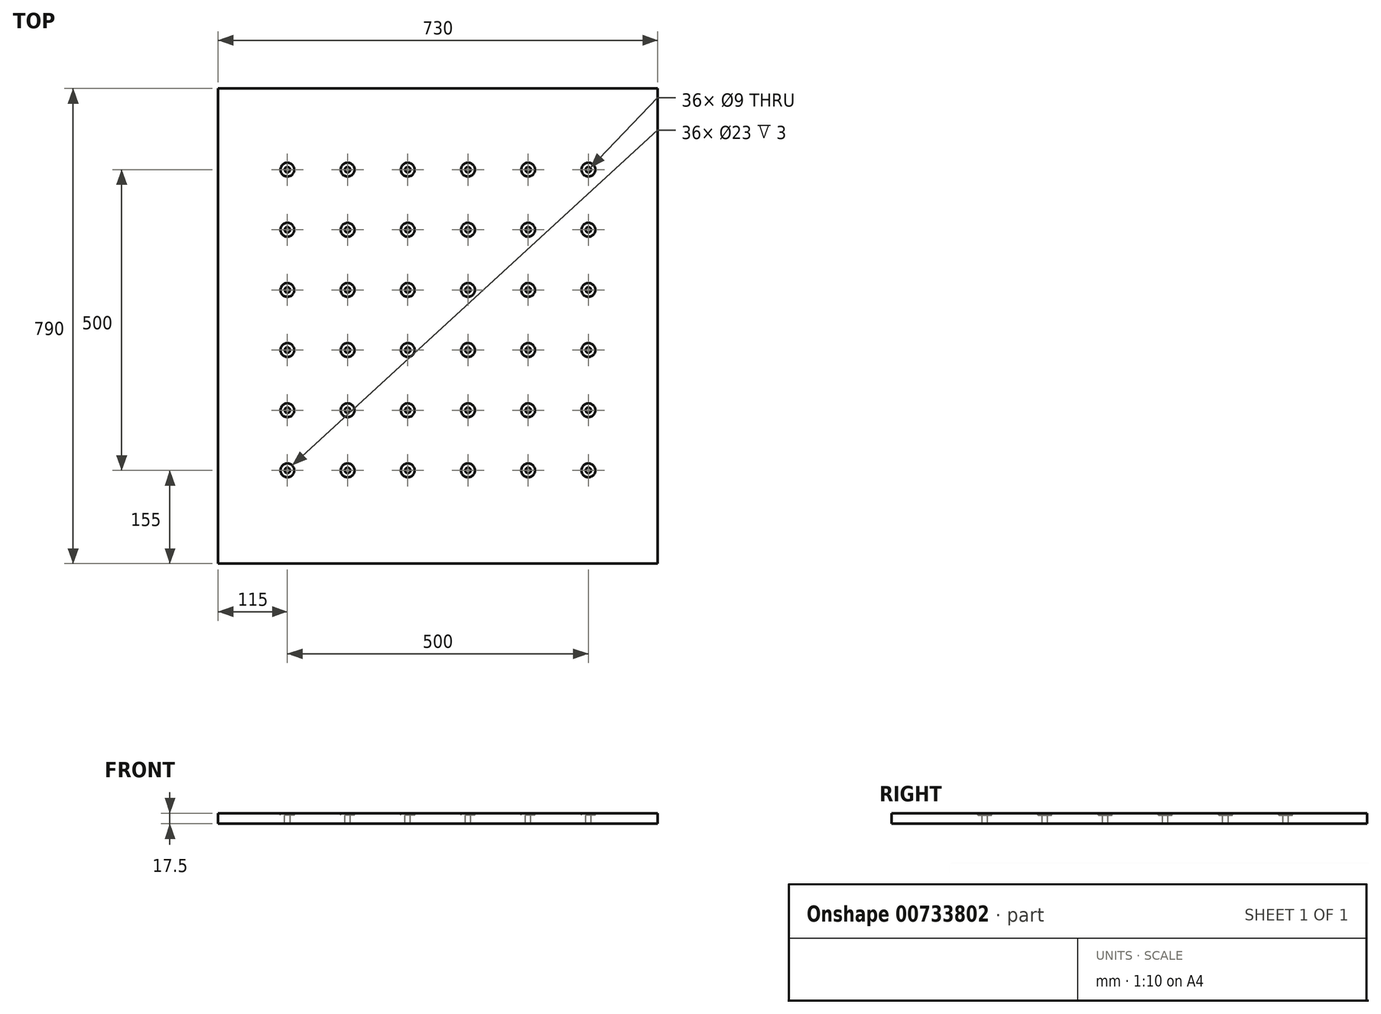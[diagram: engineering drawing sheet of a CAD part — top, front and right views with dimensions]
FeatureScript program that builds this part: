
annotation { "Feature Type Name" : "Feature", "Feature Type Description" : "" }
export const myFeature = defineFeature(function(context is Context, id is Id, definition is map)
    precondition{}
    {
        {
            var Q0;
            Q0=qCreatedBy(makeId("Top.planeOp"),FACE);
            var sketch = newSketch(context, id + "F0", { "sketchPlane" : qUnion([Q0])});
            skLineSegment(sketch, "E0.bottom", {"start": v(365, -395) * mm, "end": v(-365, -395) * mm});
            skLineSegment(sketch, "E0.top", {"start": v(365, 395) * mm, "end": v(-365, 395) * mm});
            skLineSegment(sketch, "E0.left", {"start": v(365, -395) * mm, "end": v(365, 395) * mm});
            skLineSegment(sketch, "E0.right", {"start": v(-365, -395) * mm, "end": v(-365, 395) * mm});
            skPoint(sketch, "E0.middle", {"position": v(0, 0) * mm});
            skSolve(sketch);
        }
        {
            var Q0;
            Q0 = qSketchRegion(id + "F0", true);
            extrude(context, id + "F1", {"entities" : qUnion([Q0]), "depth" : 17.5 * mm, "offsetDistance" : 25 * mm});
        }
        {
            var Q0;
            Q0=makeQuery(id+"F1.opExtrude","CAP_FACE",FACE,{"disambiguationData":[OSD([sQuery(id+"F0.wireOp",EDGE,"E0.bottom"),sQuery(id+"F0.wireOp",EDGE,"E0.top"),sQuery(id+"F0.wireOp",EDGE,"E0.left"),sQuery(id+"F0.wireOp",EDGE,"E0.right")])],"isStart":false});
            var sketch = newSketch(context, id + "F2", { "sketchPlane" : qUnion([Q0])});
            skPoint(sketch, "E1", {"position": v(-250, 260) * mm});
            skPoint(sketch, "E2.0.1.0", {"position": v(-250, 160) * mm});
            skPoint(sketch, "E2.0.2.0", {"position": v(-250, 60) * mm});
            skPoint(sketch, "E2.0.3.0", {"position": v(-250, -40) * mm});
            skPoint(sketch, "E2.0.4.0", {"position": v(-250, -140) * mm});
            skPoint(sketch, "E2.1.0.0", {"position": v(-150, 260) * mm});
            skPoint(sketch, "E2.1.1.0", {"position": v(-150, 160) * mm});
            skPoint(sketch, "E2.1.2.0", {"position": v(-150, 60) * mm});
            skPoint(sketch, "E2.1.3.0", {"position": v(-150, -40) * mm});
            skPoint(sketch, "E2.1.4.0", {"position": v(-150, -140) * mm});
            skPoint(sketch, "E2.2.0.0", {"position": v(-50, 260) * mm});
            skPoint(sketch, "E2.2.1.0", {"position": v(-50, 160) * mm});
            skPoint(sketch, "E2.2.2.0", {"position": v(-50, 60) * mm});
            skPoint(sketch, "E2.2.3.0", {"position": v(-50, -40) * mm});
            skPoint(sketch, "E2.2.4.0", {"position": v(-50, -140) * mm});
            skPoint(sketch, "E2.3.0.0", {"position": v(50, 260) * mm});
            skPoint(sketch, "E2.3.1.0", {"position": v(50, 160) * mm});
            skPoint(sketch, "E2.3.2.0", {"position": v(50, 60) * mm});
            skPoint(sketch, "E2.3.3.0", {"position": v(50, -40) * mm});
            skPoint(sketch, "E2.3.4.0", {"position": v(50, -140) * mm});
            skPoint(sketch, "E2.4.0.0", {"position": v(150, 260) * mm});
            skPoint(sketch, "E2.4.1.0", {"position": v(150, 160) * mm});
            skPoint(sketch, "E2.4.2.0", {"position": v(150, 60) * mm});
            skPoint(sketch, "E2.4.3.0", {"position": v(150, -40) * mm});
            skPoint(sketch, "E2.4.4.0", {"position": v(150, -140) * mm});
            skLineSegment(sketch, "E2.direction1", {"start": v(-250, 260) * mm, "end": v(-150, 260) * mm, "construction": true});
            skLineSegment(sketch, "E2.direction2", {"start": v(-250, 260) * mm, "end": v(-250, 160) * mm, "construction": true});
            skPoint(sketch, "E3.0.5.0", {"position": v(250, 260) * mm});
            skPoint(sketch, "E3.0.5.1", {"position": v(250, 160) * mm});
            skPoint(sketch, "E3.0.5.2", {"position": v(250, 60) * mm});
            skPoint(sketch, "E3.0.5.3", {"position": v(250, -40) * mm});
            skPoint(sketch, "E3.0.5.4", {"position": v(250, -140) * mm});
            skPoint(sketch, "E4.0.0.5", {"position": v(-250, -240) * mm});
            skPoint(sketch, "E4.0.1.5", {"position": v(-150, -240) * mm});
            skPoint(sketch, "E4.0.2.5", {"position": v(-50, -240) * mm});
            skPoint(sketch, "E4.0.3.5", {"position": v(50, -240) * mm});
            skPoint(sketch, "E4.0.4.5", {"position": v(150, -240) * mm});
            skPoint(sketch, "E4.0.5.5", {"position": v(250, -240) * mm});
            skSolve(sketch);
        }
        {
            var Q0;
            Q0=sQuery(id+"F2.wireOp",VERTEX,"E1");
            var Q1;
            Q1=sQuery(id+"F2.wireOp",VERTEX,"E2.1.0.0");
            var Q2;
            Q2=sQuery(id+"F2.wireOp",VERTEX,"E2.2.0.0");
            var Q3;
            Q3=sQuery(id+"F2.wireOp",VERTEX,"E2.3.0.0");
            var Q4;
            Q4=sQuery(id+"F2.wireOp",VERTEX,"E2.4.0.0");
            var Q5;
            Q5=sQuery(id+"F2.wireOp",VERTEX,"E2.5.0.0");
            var Q6;
            Q6=sQuery(id+"F2.wireOp",VERTEX,"E2.1.1.0");
            var Q7;
            Q7=sQuery(id+"F2.wireOp",VERTEX,"E2.0.2.0");
            var Q8;
            Q8=sQuery(id+"F2.wireOp",VERTEX,"E2.0.1.0");
            var Q9;
            Q9=sQuery(id+"F2.wireOp",VERTEX,"E2.1.5.0");
            var Q10;
            Q10=sQuery(id+"F2.wireOp",VERTEX,"E2.4.2.0");
            var Q11;
            Q11=sQuery(id+"F2.wireOp",VERTEX,"E2.1.4.0");
            var Q12;
            Q12=sQuery(id+"F2.wireOp",VERTEX,"E2.0.6.0");
            var Q13;
            Q13=sQuery(id+"F2.wireOp",VERTEX,"E2.1.3.0");
            var Q14;
            Q14=sQuery(id+"F2.wireOp",VERTEX,"E2.4.4.0");
            var Q15;
            Q15=sQuery(id+"F2.wireOp",VERTEX,"E2.0.5.0");
            var Q16;
            Q16=sQuery(id+"F2.wireOp",VERTEX,"E2.3.4.0");
            var Q17;
            Q17=sQuery(id+"F2.wireOp",VERTEX,"E2.1.2.0");
            var Q18;
            Q18=sQuery(id+"F2.wireOp",VERTEX,"E2.5.6.0");
            var Q19;
            Q19=sQuery(id+"F2.wireOp",VERTEX,"E2.2.2.0");
            var Q20;
            Q20=sQuery(id+"F2.wireOp",VERTEX,"E2.3.6.0");
            var Q21;
            Q21=sQuery(id+"F2.wireOp",VERTEX,"E2.4.6.0");
            var Q22;
            Q22=sQuery(id+"F2.wireOp",VERTEX,"E2.2.4.0");
            var Q23;
            Q23=sQuery(id+"F2.wireOp",VERTEX,"E2.2.6.0");
            var Q24;
            Q24=sQuery(id+"F2.wireOp",VERTEX,"E2.0.4.0");
            var Q25;
            Q25=sQuery(id+"F2.wireOp",VERTEX,"E2.5.1.0");
            var Q26;
            Q26=sQuery(id+"F2.wireOp",VERTEX,"E2.3.1.0");
            var Q27;
            Q27=sQuery(id+"F2.wireOp",VERTEX,"E2.5.3.0");
            var Q28;
            Q28=sQuery(id+"F2.wireOp",VERTEX,"E2.3.3.0");
            var Q29;
            Q29=sQuery(id+"F2.wireOp",VERTEX,"E2.5.5.0");
            var Q30;
            Q30=sQuery(id+"F2.wireOp",VERTEX,"E2.0.3.0");
            var Q31;
            Q31=sQuery(id+"F2.wireOp",VERTEX,"E2.4.1.0");
            var Q32;
            Q32=sQuery(id+"F2.wireOp",VERTEX,"E2.1.6.0");
            var Q33;
            Q33=sQuery(id+"F2.wireOp",VERTEX,"E2.4.3.0");
            var Q34;
            Q34=sQuery(id+"F2.wireOp",VERTEX,"E2.2.1.0");
            var Q35;
            Q35=sQuery(id+"F2.wireOp",VERTEX,"E2.4.5.0");
            var Q36;
            Q36=sQuery(id+"F2.wireOp",VERTEX,"E2.3.5.0");
            var Q37;
            Q37=sQuery(id+"F2.wireOp",VERTEX,"E2.2.3.0");
            var Q38;
            Q38=sQuery(id+"F2.wireOp",VERTEX,"E2.2.5.0");
            var Q39;
            Q39=sQuery(id+"F2.wireOp",VERTEX,"E2.5.2.0");
            var Q40;
            Q40=sQuery(id+"F2.wireOp",VERTEX,"E2.5.4.0");
            var Q41;
            Q41=sQuery(id+"F2.wireOp",VERTEX,"E2.3.2.0");
            var Q42;
            Q42=sQuery(id+"F2.wireOp",VERTEX,"E3.0.5.0");
            var Q43;
            Q43=sQuery(id+"F2.wireOp",VERTEX,"E3.0.5.1");
            var Q44;
            Q44=sQuery(id+"F2.wireOp",VERTEX,"E3.0.5.2");
            var Q45;
            Q45=sQuery(id+"F2.wireOp",VERTEX,"E3.0.5.3");
            var Q46;
            Q46=sQuery(id+"F2.wireOp",VERTEX,"E3.0.5.4");
            var Q47;
            Q47=sQuery(id+"F2.wireOp",VERTEX,"E4.0.5.5");
            var Q48;
            Q48=sQuery(id+"F2.wireOp",VERTEX,"E4.0.4.5");
            var Q49;
            Q49=sQuery(id+"F2.wireOp",VERTEX,"E4.0.3.5");
            var Q50;
            Q50=sQuery(id+"F2.wireOp",VERTEX,"E4.0.2.5");
            var Q51;
            Q51=sQuery(id+"F2.wireOp",VERTEX,"E4.0.1.5");
            var Q52;
            Q52=sQuery(id+"F2.wireOp",VERTEX,"E4.0.0.5");
            var Q53;
            Q53=makeQuery(id+"F1.opExtrude","SWEPT_BODY",BODY,{"disambiguationData":[OSD([sQuery(id+"F0.wireOp",EDGE,"E0.bottom"),sQuery(id+"F0.wireOp",EDGE,"E0.top"),sQuery(id+"F0.wireOp",EDGE,"E0.left"),sQuery(id+"F0.wireOp",EDGE,"E0.right")])]});
            hole(context, id + "F3", {"style" : HoleStyle.C_BORE, "endStyle" : HoleEndStyle.THROUGH, "holeDiameter" : 9 * mm, "cBoreDiameter" : 23 * mm, "cBoreDepth" : 3 * mm, "majorDiameter" : 12 * mm, "tappedDepth" : 7.6 * mm, "tapClearance" : 3, "startFromSketch" : true, "locations" : qUnion([Q0, Q1, Q2, Q3, Q4, Q5, Q6, Q7, Q8, Q9, Q10, Q11, Q12, Q13, Q14, Q15, Q16, Q17, Q18, Q19, Q20, Q21, Q22, Q23, Q24, Q25, Q26, Q27, Q28, Q29, Q30, Q31, Q32, Q33, Q34, Q35, Q36, Q37, Q38, Q39, Q40, Q41, Q42, Q43, Q44, Q45, Q46, Q47, Q48, Q49, Q50, Q51, Q52]), "scope" : qUnion([Q53])});
        }
    });
